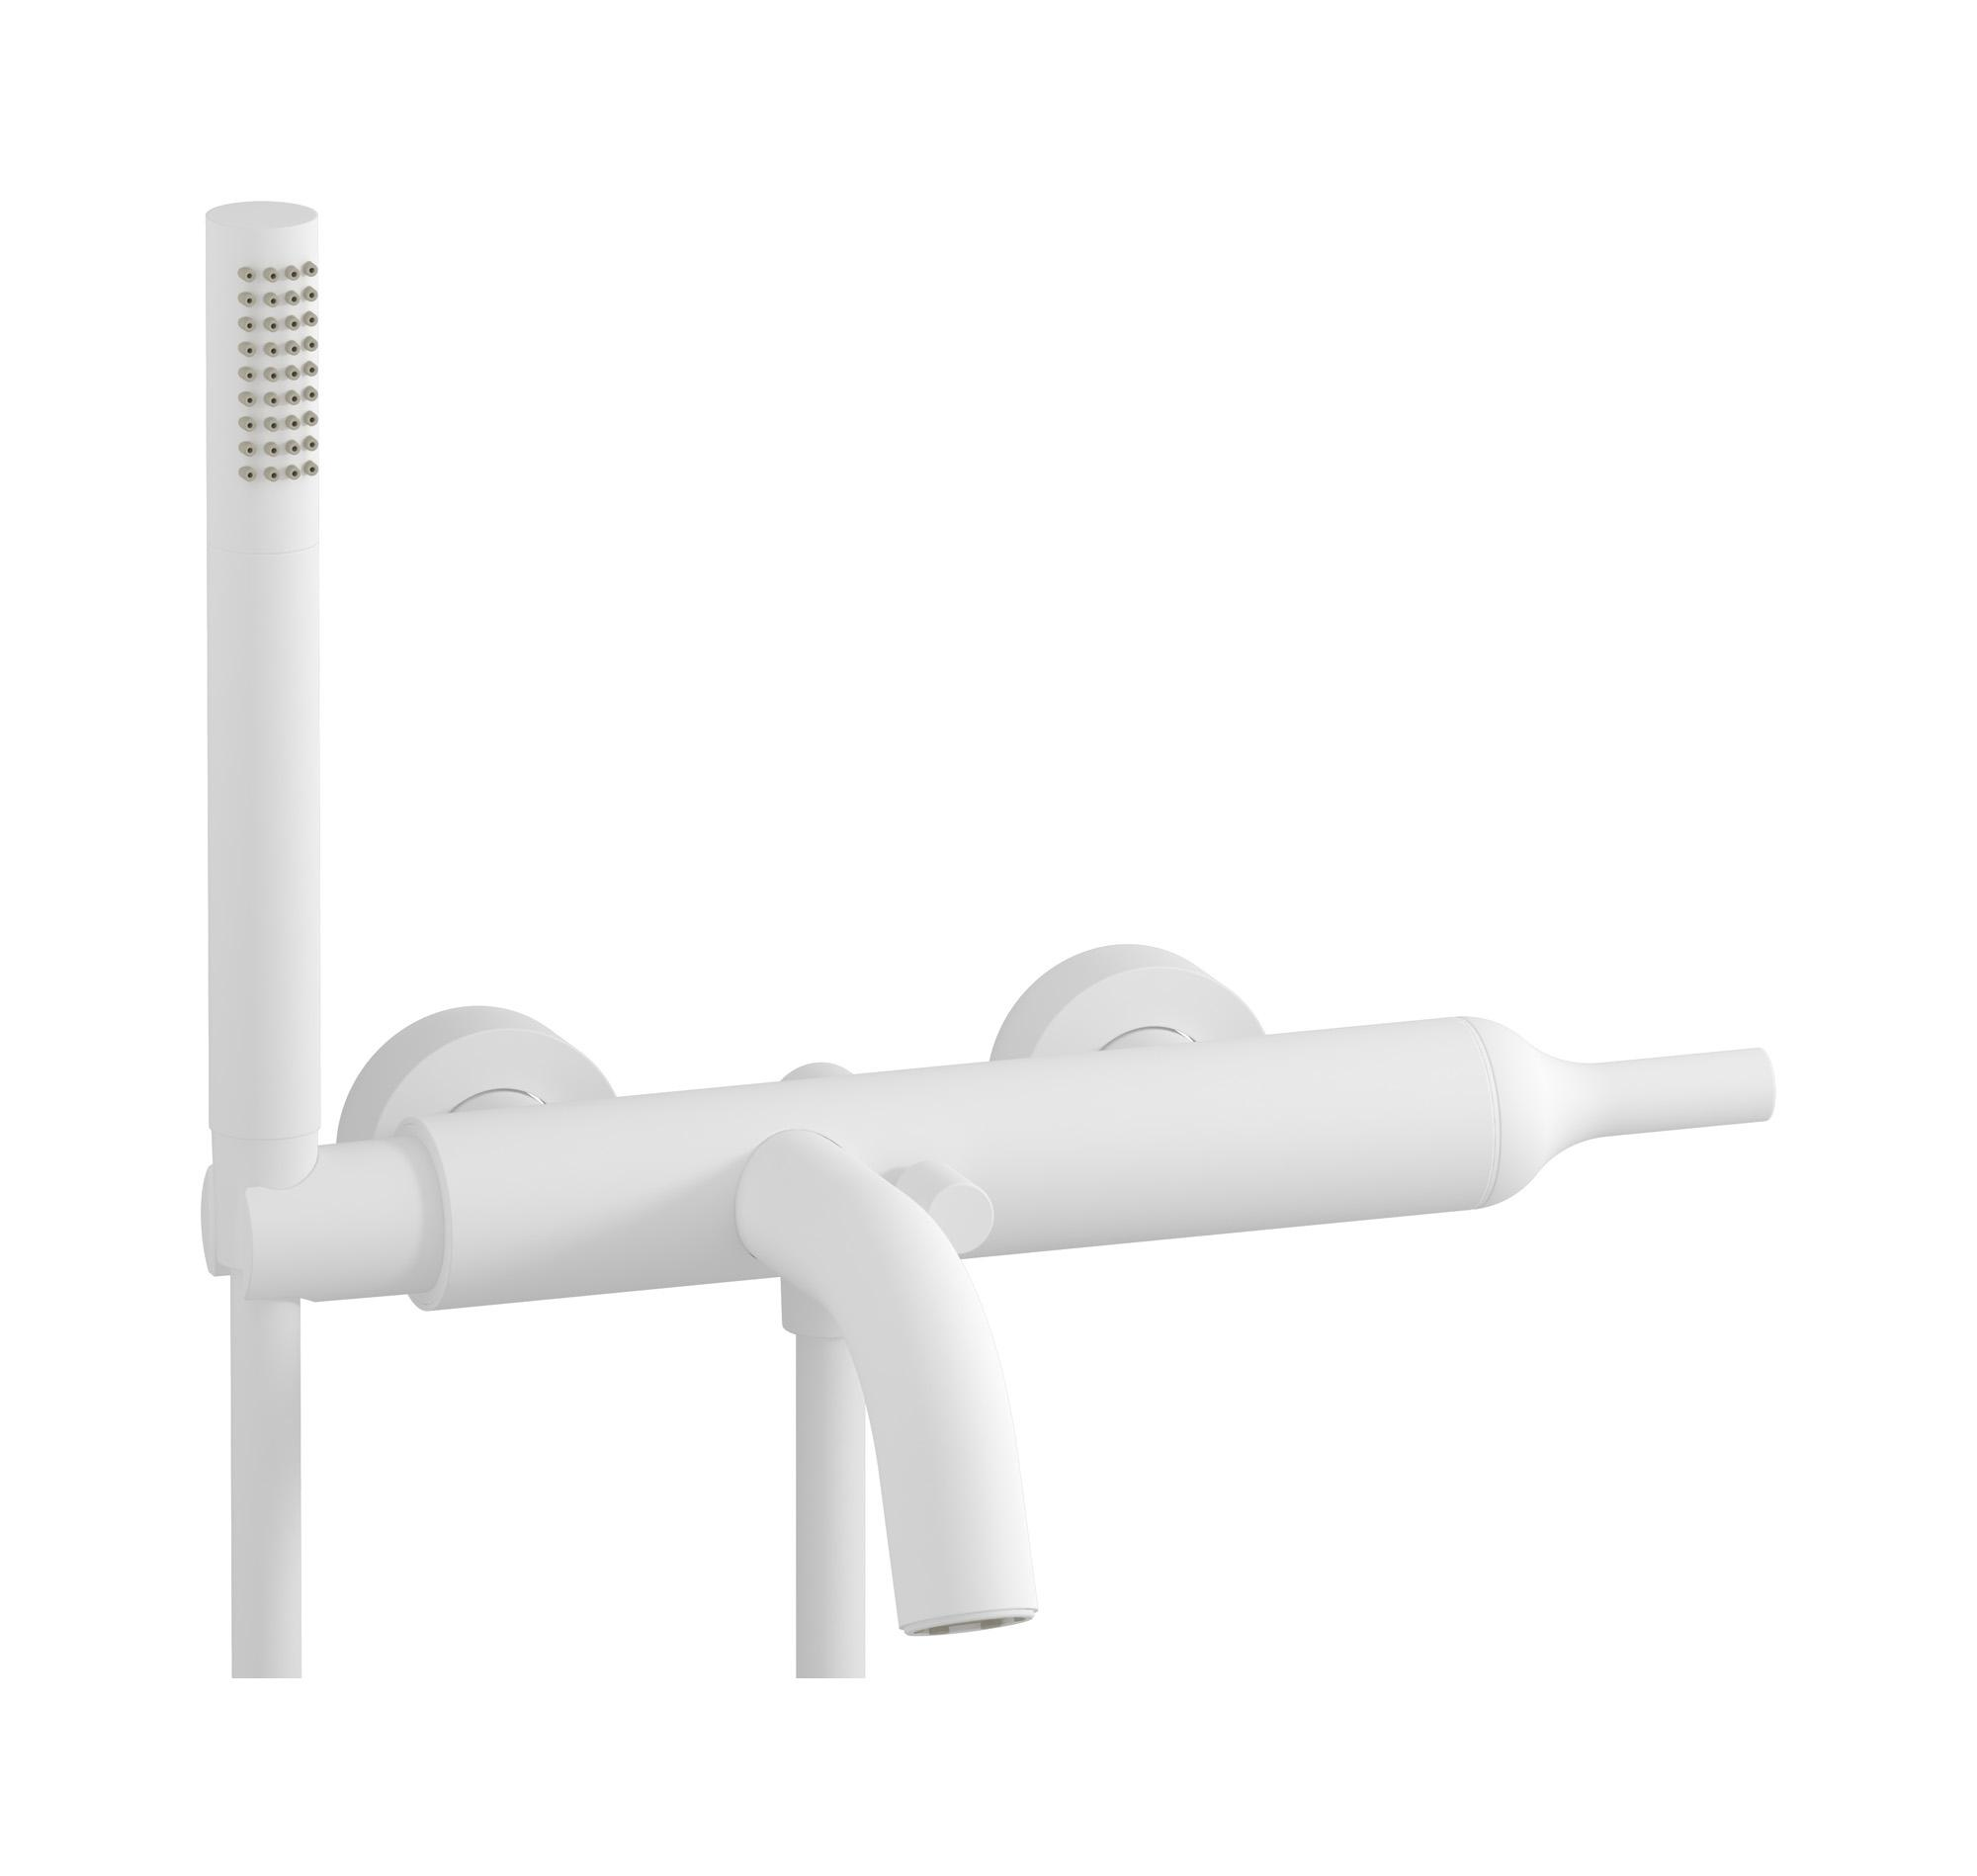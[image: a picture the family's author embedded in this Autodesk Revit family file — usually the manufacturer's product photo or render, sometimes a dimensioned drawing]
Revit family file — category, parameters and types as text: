
# Revit family: BI250
name_source: partatom
category: Apparecchi idraulici
units: mm (PartAtom-declared; Revit-internal decimal feet)

## family parameters
Basato su piano di lavoro = No
Condiviso = No
Mantieni orientamento annotazione = No
Numero OmniClass = 23.45.55.17
Punto di calcolo locali = No
Quota connettore circolare = Usa diametro
Sempre verticale = Sì
Taglio con vuoti quando caricato = No
Tipo di parte = Normale
Titolo OmniClass = Mixing Faucets

## types (4) — shared parameters
Cold water inlet = 10 mm  [stored 0.0328084 ft]
Commenti sul tipo = Bath filler
Connessione CW = No
Connessione HW = No
Connessione di scarico = No
Connessione di ventilazione = No
Descrizione = Wall mounted bath filler complete with shower kit
Hot water inlet = 10 mm  [stored 0.0328084 ft]
Produttore = IB Rubinetterie S.p.A.
URL = https://www.weareib.it
zero-valued in all types: Prospetto di default

## per-type parameters (varying)
| type | Finishes surface | Immagine tipo | Modello |
| Chrome | IB_Chrome | BI250CC.jpg | BI250CC |
| Brushed nickel | IB_Brushed nickel | BI250SS.jpg | BI250SS |
| Matt black | IB_matt black | BI250NP.jpg | BI250NP |
| Matt white | IB_matt white | BI250BO.jpg | BI250BO |

note: [stored X ft] marks values corroborated as IEEE doubles in the binary element streams (Revit-internal decimal feet)
